FCSTD DOCUMENT  (FreeCAD 0.16RUnknown)
Label: marine18
License: All rights reserved
LicenseURL: http://en.wikipedia.org/wiki/All_rights_reserved
objects: Sketcher::SketchObject×1
note: 1 computed .brp shape members not serialized (recipe doc carries the construction recipe); baked Part::Feature solids carry a one-line shape summary decoded from their .brp

FEATURE [Sketcher::SketchObject] Sketch  label="test"
  sketch-geometry (36):
    g0: LineSegment StartX=-59 StartY=110 StartZ=0 EndX=-35 EndY=110 EndZ=0
    g1: LineSegment StartX=59 StartY=110 StartZ=0 EndX=59 EndY=68.2 EndZ=0
    g2: LineSegment StartX=59 StartY=-110 StartZ=0 EndX=-59 EndY=-110 EndZ=0
    g3: LineSegment StartX=-59 StartY=-110 StartZ=0 EndX=-59 EndY=-68.2 EndZ=0
    g4: LineSegment StartX=19 StartY=68.2 StartZ=0 EndX=59 EndY=68.2 EndZ=0
    g5: LineSegment StartX=59 StartY=50.5 StartZ=0 EndX=19 EndY=50.5 EndZ=0
    g6: LineSegment StartX=19 StartY=50.5 StartZ=0 EndX=19 EndY=68.2 EndZ=0
    g7: LineSegment StartX=19 StartY=8.7 StartZ=0 EndX=59 EndY=8.7 EndZ=0
    g8: LineSegment StartX=59 StartY=-8.9 StartZ=0 EndX=19 EndY=-8.9 EndZ=0
    g9: LineSegment StartX=19 StartY=-8.9 StartZ=0 EndX=19 EndY=8.7 EndZ=0
    g10: LineSegment StartX=19 StartY=-50.7 StartZ=0 EndX=59 EndY=-50.7 EndZ=0
    g11: LineSegment StartX=59 StartY=-68.2 StartZ=0 EndX=19 EndY=-68.2 EndZ=0
    g12: LineSegment StartX=19 StartY=-68.2 StartZ=0 EndX=19 EndY=-50.7 EndZ=0
    g13: LineSegment StartX=-59 StartY=68.2 StartZ=0 EndX=-19 EndY=68.2 EndZ=0
    g14: LineSegment StartX=-19 StartY=68.2 StartZ=0 EndX=-19 EndY=50.2 EndZ=0
    g15: LineSegment StartX=-19 StartY=50.2 StartZ=0 EndX=-59 EndY=50.2 EndZ=0
    g16: LineSegment StartX=-59 StartY=8.4 StartZ=0 EndX=-19 EndY=8.4 EndZ=0
    g17: LineSegment StartX=-19 StartY=8.4 StartZ=0 EndX=-19 EndY=-9 EndZ=0
    g18: LineSegment StartX=-19 StartY=-9 StartZ=0 EndX=-59 EndY=-9 EndZ=0
    g19: LineSegment StartX=-59 StartY=-50.8 StartZ=0 EndX=-19 EndY=-50.8 EndZ=0
    g20: LineSegment StartX=-19 StartY=-50.8 StartZ=0 EndX=-19 EndY=-68.2 EndZ=0
    g21: LineSegment StartX=-19 StartY=-68.2 StartZ=0 EndX=-59 EndY=-68.2 EndZ=0
    g22: LineSegment StartX=59 StartY=50.5 StartZ=0 EndX=59 EndY=8.7 EndZ=0
    g23: LineSegment StartX=59 StartY=-8.9 StartZ=0 EndX=59 EndY=-50.7 EndZ=0
    g24: LineSegment StartX=59 StartY=-68.2 StartZ=0 EndX=59 EndY=-110 EndZ=0
    g25: LineSegment StartX=-59 StartY=68.2 StartZ=0 EndX=-59 EndY=110 EndZ=0
    g26: LineSegment StartX=-59 StartY=8.4 StartZ=0 EndX=-59 EndY=50.2 EndZ=0
    g27: LineSegment StartX=-59 StartY=-50.8 StartZ=0 EndX=-59 EndY=-9 EndZ=0
    g28: LineSegment StartX=35 StartY=110 StartZ=0 EndX=35 EndY=92 EndZ=0
    g29: LineSegment StartX=35 StartY=92 StartZ=0 EndX=-35 EndY=92 EndZ=0
    g30: LineSegment StartX=-35 StartY=92 StartZ=0 EndX=-35 EndY=110 EndZ=0
    g31: LineSegment StartX=35 StartY=110 StartZ=0 EndX=59 EndY=110 EndZ=0
    g32: LineSegment StartX=-34.8 StartY=-82.4 StartZ=0 EndX=34.8 EndY=-82.4 EndZ=0
    g33: LineSegment StartX=34.8 StartY=-82.4 StartZ=0 EndX=34.8 EndY=-100 EndZ=0
    g34: LineSegment StartX=34.8 StartY=-100 StartZ=0 EndX=-34.8 EndY=-100 EndZ=0
    g35: LineSegment StartX=-34.8 StartY=-100 StartZ=0 EndX=-34.8 EndY=-82.4 EndZ=0
  constraints (101):
    c: Coincident(g31,g1)
    c: Coincident(g24,g2)
    c: Coincident(g2,g3)
    c: Coincident(g25,g0)
    c: Horizontal(g2)
    c: Vertical(g1)
    c: Vertical(g3)
    c: DistanceY(g3,g25) = 220
    c: DistanceX(g2,g2) = 118
    c: Symmetric(g0,g31,g-2)
    c: Symmetric(g0,g2,g-1)
    c: Coincident(g5,g6)
    c: Coincident(g6,g4)
    c: Horizontal(g4)
    c: Horizontal(g5)
    c: Vertical(g6)
    c: Coincident(g8,g9)
    c: Coincident(g9,g7)
    c: Horizontal(g7)
    c: Horizontal(g8)
    c: Vertical(g9)
    c: Coincident(g11,g12)
    c: Coincident(g12,g10)
    c: Horizontal(g10)
    c: Horizontal(g11)
    c: Vertical(g12)
    c: DistanceY(g6,g6) = 17.7
    c: DistanceY(g9,g9) = 17.6
    c: DistanceY(g12,g12) = 17.5
    c: Coincident(g13,g14)
    c: Coincident(g14,g15)
    c: Horizontal(g13)
    c: Horizontal(g15)
    c: Vertical(g14)
    c: Coincident(g16,g17)
    c: Coincident(g17,g18)
    c: Horizontal(g16)
    c: Horizontal(g18)
    c: Vertical(g17)
    c: Coincident(g19,g20)
    c: Coincident(g20,g21)
    c: Horizontal(g19)
    c: Horizontal(g21)
    c: Vertical(g20)
    c: DistanceY(g14,g14) = 18
    c: DistanceY(g17,g17) = 17.4
    c: DistanceY(g20,g20) = 17.4
    c: Tangent(g1,g22)
    c: Tangent(g22,g23)
    c: Tangent(g23,g24)
    c: Coincident(g10,g23)
    c: Coincident(g11,g24)
    c: Coincident(g8,g23)
    c: Coincident(g7,g22)
    c: Coincident(g5,g22)
    c: Coincident(g4,g1)
    c: Tangent(g3,g25)
    c: Tangent(g3,g26)
    c: Tangent(g3,g27)
    c: Coincident(g13,g25)
    c: Coincident(g15,g26)
    c: Coincident(g16,g26)
    c: Coincident(g18,g27)
    c: Coincident(g19,g27)
    c: Coincident(g21,g3)
    c: Equal(g1,g22)
    c: Equal(g22,g23)
    c: Equal(g23,g24)
    c: Equal(g24,g3)
    c: Equal(g3,g27)
    c: Equal(g27,g26)
    c: Equal(g26,g25)
    c: Equal(g5,g8)
    c: Equal(g8,g11)
    c: Equal(g11,g21)
    c: Equal(g21,g18)
    c: Equal(g18,g15)
    c: DistanceX(g4,g4) = 40
    c: Coincident(g28,g29)
    c: Coincident(g29,g30)
    c: Horizontal(g29)
    c: Vertical(g28)
    c: Vertical(g30)
    c: Tangent(g0,g31)
    c: Coincident(g28,g31)
    c: Coincident(g30,g0)
    c: DistanceX(g29,g29) = 70
    c: DistanceY(g28,g28) = 18
    c: Equal(g31,g0)
    c: Coincident(g32,g33)
    c: Coincident(g33,g34)
    c: Coincident(g34,g35)
    c: Coincident(g35,g32)
    c: Horizontal(g32)
    c: Horizontal(g34)
    c: Vertical(g33)
    c: Vertical(g35)
    c: DistanceX(g34,g34) = 69.6
    c: DistanceY(g33,g33) = 17.6
    c: Symmetric(g32,g32,g-2)
    c: Distance(g33,g2) = 10
